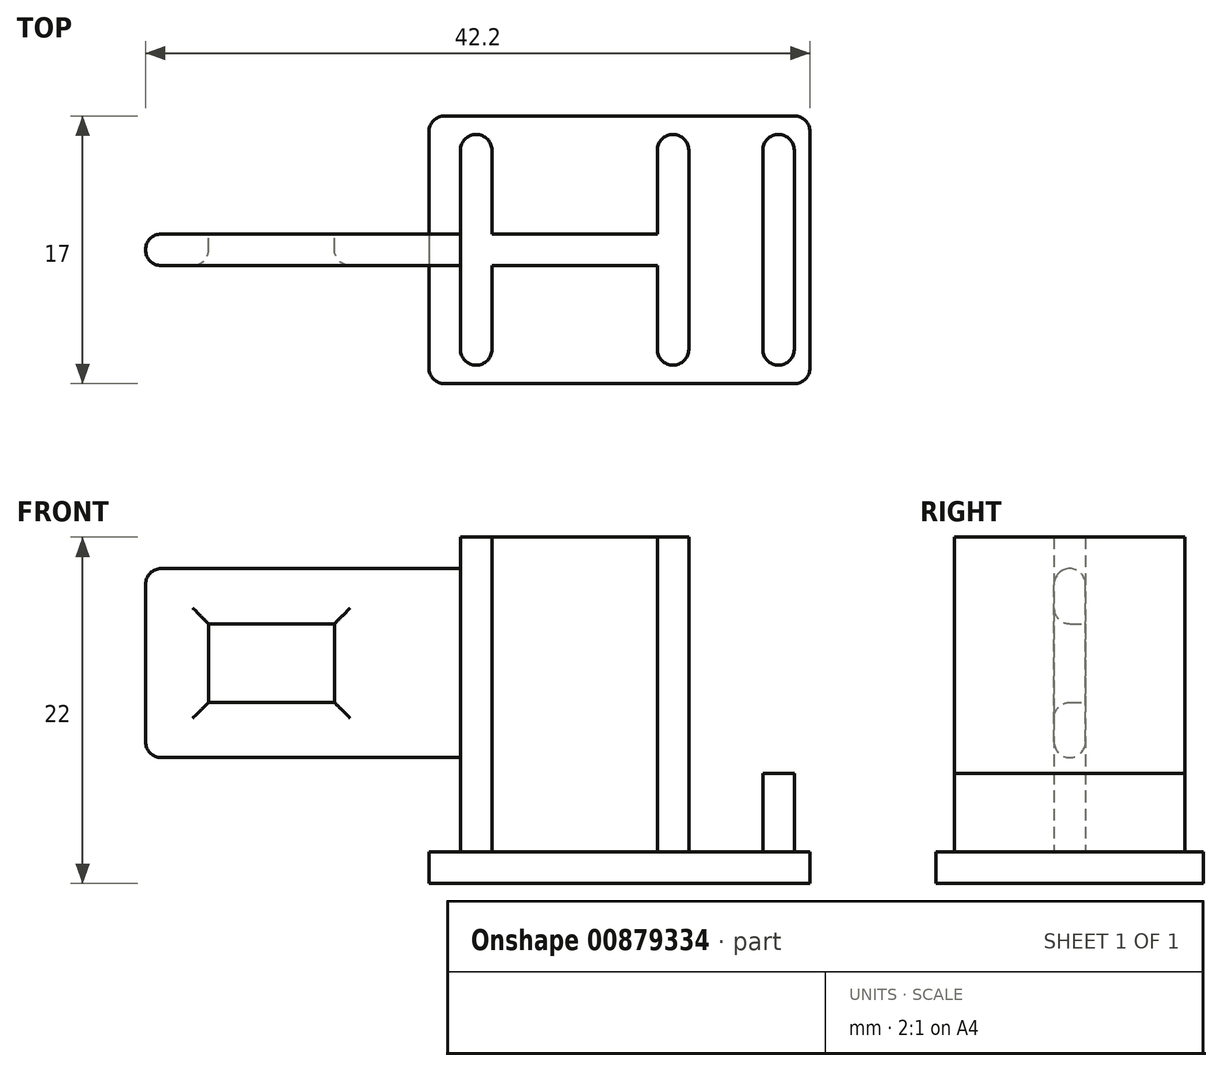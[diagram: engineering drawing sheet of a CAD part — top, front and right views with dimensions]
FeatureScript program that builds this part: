
annotation { "Feature Type Name" : "Feature", "Feature Type Description" : "" }
export const myFeature = defineFeature(function(context is Context, id is Id, definition is map)
    precondition{}
    {
        {
            var Q0;
            Q0=qCreatedBy(makeId("Top.planeOp"),FACE);
            var sketch = newSketch(context, id + "F0", { "sketchPlane" : qUnion([Q0])});
            skLineSegment(sketch, "E0.bottom", {"start": v(12.1, 8.5) * mm, "end": v(-12.1, 8.5) * mm});
            skLineSegment(sketch, "E0.top", {"start": v(12.1, -8.5) * mm, "end": v(-12.1, -8.5) * mm});
            skLineSegment(sketch, "E0.left", {"start": v(12.1, 8.5) * mm, "end": v(12.1, -8.5) * mm});
            skLineSegment(sketch, "E0.right", {"start": v(-12.1, 8.5) * mm, "end": v(-12.1, -8.5) * mm});
            skPoint(sketch, "E0.middle", {"position": v(0, 0) * mm});
            skLineSegment(sketch, "E1.bottom", {"start": v(9.1, 7.33) * mm, "end": v(11.1, 7.33) * mm});
            skLineSegment(sketch, "E1.top", {"start": v(9.1, -7.32) * mm, "end": v(11.1, -7.32) * mm});
            skLineSegment(sketch, "E1.left", {"start": v(9.1, 7.33) * mm, "end": v(9.1, -7.32) * mm});
            skLineSegment(sketch, "E1.right", {"start": v(11.1, 7.33) * mm, "end": v(11.1, -7.32) * mm});
            skPoint(sketch, "E1.middle", {"position": v(10.1, 0) * mm});
            skLineSegment(sketch, "E2.bottom", {"start": v(-8.1, 7.32) * mm, "end": v(-10.1, 7.32) * mm});
            skLineSegment(sketch, "E2.top", {"start": v(-8.1, -7.33) * mm, "end": v(-10.1, -7.33) * mm});
            skLineSegment(sketch, "E2.left", {"start": v(-8.1, 7.32) * mm, "end": v(-8.1, -7.33) * mm});
            skLineSegment(sketch, "E2.right", {"start": v(-10.1, 7.33) * mm, "end": v(-10.1, -7.33) * mm});
            skPoint(sketch, "E2.middle", {"position": v(-9.1, 0) * mm});
            skLineSegment(sketch, "E3.bottom", {"start": v(2.4, 7.33) * mm, "end": v(4.4, 7.33) * mm});
            skLineSegment(sketch, "E3.top", {"start": v(2.4, -7.32) * mm, "end": v(4.4, -7.32) * mm});
            skLineSegment(sketch, "E3.left", {"start": v(2.4, 7.33) * mm, "end": v(2.4, -7.32) * mm});
            skLineSegment(sketch, "E3.right", {"start": v(4.4, 7.33) * mm, "end": v(4.4, -7.32) * mm});
            skPoint(sketch, "E3.middle", {"position": v(3.4, 0) * mm});
            skLineSegment(sketch, "E4.bottom", {"start": v(-8.1, 1) * mm, "end": v(2.4, 1) * mm});
            skLineSegment(sketch, "E4.top", {"start": v(-8.1, -1) * mm, "end": v(2.4, -1) * mm});
            skLineSegment(sketch, "E4.left", {"start": v(-8.1, 1) * mm, "end": v(-8.1, -1) * mm});
            skLineSegment(sketch, "E4.right", {"start": v(2.4, 1) * mm, "end": v(2.4, -1) * mm});
            skPoint(sketch, "E4.middle", {"position": v(-2.85, 0) * mm});
            skLineSegment(sketch, "E5", {"start": v(2.4, 0) * mm, "end": v(-8.1, 0) * mm});
            skSolve(sketch);
        }
        {
            var Q0;
            Q0=makeQuery(id+"F0.imprint","IMPRINT",FACE,{"disambiguationData":[TD([[makeQuery(id+"F0.imprint","IMPRINT",EDGE,{"derivedFrom":sQuery(id+"F0.wireOp",EDGE,"E0.bottom")}),1.0]])]});
            var Q1;
            Q1=makeQuery(id+"F0.imprint","IMPRINT",FACE,{"disambiguationData":[TD([[makeQuery(id+"F0.imprint","IMPRINT",EDGE,{"derivedFrom":sQuery(id+"F0.wireOp",EDGE,"E2.bottom")}),1.0]])]});
            var Q2;
            Q2=makeQuery(id+"F0.imprint","IMPRINT",FACE,{"disambiguationData":[TD([[makeQuery(id+"F0.imprint","IMPRINT",EDGE,{"derivedFrom":sQuery(id+"F0.wireOp",EDGE,"E3.bottom")}),-1.0]])]});
            var Q3;
            Q3=makeQuery(id+"F0.imprint","IMPRINT",FACE,{"disambiguationData":[TD([[makeQuery(id+"F0.imprint","IMPRINT",EDGE,{"derivedFrom":sQuery(id+"F0.wireOp",EDGE,"E1.bottom")}),-1.0]])]});
            var Q4;
            {var subQ0=sQuery(id+"F0.wireOp",EDGE,"E4.top");Q4=makeQuery(id+"F0.imprint","IMPRINT",FACE,{"disambiguationData":[TD([[makeQuery(id+"F0.imprint","IMPRINT",EDGE,{"derivedFrom":subQ0}),1.0]])]});}
            var Q5;
            {var subQ0=sQuery(id+"F0.wireOp",EDGE,"E4.bottom");Q5=makeQuery(id+"F0.imprint","IMPRINT",FACE,{"disambiguationData":[TD([[makeQuery(id+"F0.imprint","IMPRINT",EDGE,{"derivedFrom":subQ0}),-1.0]])]});}
            extrude(context, id + "F1", {"entities" : qUnion([Q0, Q1, Q2, Q3, Q4, Q5]), "oppositeDirection" : true, "depth" : 2 * mm, "offsetDistance" : 25 * mm});
        }
        {
            var Q0;
            {var subQ4=sQuery(id+"F0.wireOp",EDGE,"E2.bottom");Q0=makeQuery(id+"F0.imprint","IMPRINT",FACE,{"disambiguationData":[TD([[makeQuery(id+"F0.imprint","IMPRINT",EDGE,{"derivedFrom":subQ4}),1.0]])]});}
            var Q1;
            {var subQ0=sQuery(id+"F0.wireOp",EDGE,"E4.bottom");Q1=makeQuery(id+"F0.imprint","IMPRINT",FACE,{"disambiguationData":[TD([[makeQuery(id+"F0.imprint","IMPRINT",EDGE,{"derivedFrom":subQ0}),-1.0]])]});}
            var Q2;
            {var subQ4=sQuery(id+"F0.wireOp",EDGE,"E3.bottom");Q2=makeQuery(id+"F0.imprint","IMPRINT",FACE,{"disambiguationData":[TD([[makeQuery(id+"F0.imprint","IMPRINT",EDGE,{"derivedFrom":subQ4}),-1.0]])]});}
            var Q3;
            {var subQ0=sQuery(id+"F0.wireOp",EDGE,"E4.top");Q3=makeQuery(id+"F0.imprint","IMPRINT",FACE,{"disambiguationData":[TD([[makeQuery(id+"F0.imprint","IMPRINT",EDGE,{"derivedFrom":subQ0}),1.0]])]});}
            extrude(context, id + "F2", {"entities" : qUnion([Q0, Q1, Q2, Q3]), "operationType" : NewBodyOperationType.ADD, "depth" : 20 * mm, "offsetDistance" : 25 * mm});
        }
        {
            var Q0;
            Q0=makeQuery(id+"F0.imprint","IMPRINT",FACE,{"disambiguationData":[TD([[makeQuery(id+"F0.imprint","IMPRINT",EDGE,{"derivedFrom":sQuery(id+"F0.wireOp",EDGE,"E1.bottom")}),-1.0]])]});
            extrude(context, id + "F3", {"entities" : qUnion([Q0]), "operationType" : NewBodyOperationType.ADD, "depth" : 5 * mm, "offsetDistance" : 25 * mm});
        }
        {
            var Q0;
            Q0=makeQuery(id+"F2.opExtrude","SWEPT_FACE",FACE,{"disambiguationData":[OSD([sQuery(id+"F0.wireOp",EDGE,"E2.right")])]});
            var sketch = newSketch(context, id + "F4", { "sketchPlane" : qUnion([Q0])});
            skLineSegment(sketch, "E6.bottom", {"start": v(1, 6) * mm, "end": v(-1, 6) * mm});
            skLineSegment(sketch, "E6.top", {"start": v(1, 18) * mm, "end": v(-1, 18) * mm});
            skLineSegment(sketch, "E6.left", {"start": v(1, 6) * mm, "end": v(1, 18) * mm});
            skLineSegment(sketch, "E6.right", {"start": v(-1, 6) * mm, "end": v(-1, 18) * mm});
            skPoint(sketch, "E6.middle", {"position": v(0, 12) * mm});
            skSolve(sketch);
        }
        {
            var Q0;
            Q0 = qSketchRegion(id + "F4", true);
            extrude(context, id + "F5", {"entities" : qUnion([Q0]), "operationType" : NewBodyOperationType.ADD, "depth" : 20 * mm, "offsetDistance" : 25 * mm});
        }
        {
            var Q0;
            Q0=makeQuery(id+"F5.opExtrude","SWEPT_FACE",FACE,{"disambiguationData":[OSD([sQuery(id+"F4.wireOp",EDGE,"E6.right")])]});
            var sketch = newSketch(context, id + "F6", { "sketchPlane" : qUnion([Q0])});
            skLineSegment(sketch, "E7.bottom", {"start": v(26.1, 14.5) * mm, "end": v(18.1, 14.5) * mm});
            skLineSegment(sketch, "E7.top", {"start": v(26.1, 9.5) * mm, "end": v(18.1, 9.5) * mm});
            skLineSegment(sketch, "E7.left", {"start": v(26.1, 14.5) * mm, "end": v(26.1, 9.5) * mm});
            skLineSegment(sketch, "E7.right", {"start": v(18.1, 14.5) * mm, "end": v(18.1, 9.5) * mm});
            skPoint(sketch, "E7.middle", {"position": v(22.1, 12) * mm});
            skPoint(sketch, "E7.middle.positionSnap0", {"position": v(29.1, 12) * mm});
            skPoint(sketch, "E7.centerSnap0", {"position": v(29.1, 12) * mm});
            skSolve(sketch);
        }
        {
            var Q0;
            Q0=makeQuery(id+"F6.imprint","IMPRINT",FACE,{"disambiguationData":[TD([[makeQuery(id+"F6.imprint","IMPRINT",EDGE,{"derivedFrom":sQuery(id+"F6.wireOp",EDGE,"E7.bottom")}),1.0]])]});
            extrude(context, id + "F7", {"entities" : qUnion([Q0]), "operationType" : NewBodyOperationType.REMOVE, "oppositeDirection" : true, "depth" : 25 * mm, "offsetDistance" : 25 * mm});
        }
        {
            var Q0;
            Q0=makeQuery(id+"F1.opExtrude","SWEPT_EDGE",EDGE,{"disambiguationData":[OSD([sQuery(id+"F0.wireOp",EDGE,"E0.top"),sQuery(id+"F0.wireOp",EDGE,"E0.right")])]});
            var Q1;
            Q1=makeQuery(id+"F1.opExtrude","SWEPT_EDGE",EDGE,{"disambiguationData":[OSD([sQuery(id+"F0.wireOp",EDGE,"E0.bottom"),sQuery(id+"F0.wireOp",EDGE,"E0.right")])]});
            var Q2;
            Q2=makeQuery(id+"F1.opExtrude","SWEPT_EDGE",EDGE,{"disambiguationData":[OSD([sQuery(id+"F0.wireOp",EDGE,"E0.top"),sQuery(id+"F0.wireOp",EDGE,"E0.left")])]});
            var Q3;
            Q3=makeQuery(id+"F1.opExtrude","SWEPT_EDGE",EDGE,{"disambiguationData":[OSD([sQuery(id+"F0.wireOp",EDGE,"E0.bottom"),sQuery(id+"F0.wireOp",EDGE,"E0.left")])]});
            var Q4;
            Q4=makeQuery(id+"F3.opExtrude","SWEPT_EDGE",EDGE,{"disambiguationData":[OSD([sQuery(id+"F0.wireOp",EDGE,"E1.top"),sQuery(id+"F0.wireOp",EDGE,"E1.right")])]});
            var Q5;
            Q5=makeQuery(id+"F3.opExtrude","SWEPT_EDGE",EDGE,{"disambiguationData":[OSD([sQuery(id+"F0.wireOp",EDGE,"E1.top"),sQuery(id+"F0.wireOp",EDGE,"E1.left")])]});
            var Q6;
            Q6=makeQuery(id+"F3.opExtrude","SWEPT_EDGE",EDGE,{"disambiguationData":[OSD([sQuery(id+"F0.wireOp",EDGE,"E1.bottom"),sQuery(id+"F0.wireOp",EDGE,"E1.right")])]});
            var Q7;
            Q7=makeQuery(id+"F3.opExtrude","SWEPT_EDGE",EDGE,{"disambiguationData":[OSD([sQuery(id+"F0.wireOp",EDGE,"E1.bottom"),sQuery(id+"F0.wireOp",EDGE,"E1.left")])]});
            var Q8;
            Q8=makeQuery(id+"F2.opExtrude","SWEPT_EDGE",EDGE,{"disambiguationData":[OSD([sQuery(id+"F0.wireOp",EDGE,"E3.top"),sQuery(id+"F0.wireOp",EDGE,"E3.left")])]});
            var Q9;
            Q9=makeQuery(id+"F2.opExtrude","SWEPT_EDGE",EDGE,{"disambiguationData":[OSD([sQuery(id+"F0.wireOp",EDGE,"E3.top"),sQuery(id+"F0.wireOp",EDGE,"E3.right")])]});
            var Q10;
            Q10=makeQuery(id+"F2.opExtrude","SWEPT_EDGE",EDGE,{"disambiguationData":[OSD([sQuery(id+"F0.wireOp",EDGE,"E2.top"),sQuery(id+"F0.wireOp",EDGE,"E2.left")])]});
            var Q11;
            Q11=makeQuery(id+"F2.opExtrude","SWEPT_EDGE",EDGE,{"disambiguationData":[OSD([sQuery(id+"F0.wireOp",EDGE,"E2.top"),sQuery(id+"F0.wireOp",EDGE,"E2.right")])]});
            var Q12;
            Q12=makeQuery(id+"F2.opExtrude","SWEPT_EDGE",EDGE,{"disambiguationData":[OSD([sQuery(id+"F0.wireOp",EDGE,"E2.bottom"),sQuery(id+"F0.wireOp",EDGE,"E2.right")])]});
            var Q13;
            Q13=makeQuery(id+"F2.opExtrude","SWEPT_EDGE",EDGE,{"disambiguationData":[OSD([sQuery(id+"F0.wireOp",EDGE,"E2.bottom"),sQuery(id+"F0.wireOp",EDGE,"E2.left")])]});
            var Q14;
            Q14=makeQuery(id+"F2.opExtrude","SWEPT_EDGE",EDGE,{"disambiguationData":[OSD([sQuery(id+"F0.wireOp",EDGE,"E3.bottom"),sQuery(id+"F0.wireOp",EDGE,"E3.left")])]});
            var Q15;
            Q15=makeQuery(id+"F2.opExtrude","SWEPT_EDGE",EDGE,{"disambiguationData":[OSD([sQuery(id+"F0.wireOp",EDGE,"E3.bottom"),sQuery(id+"F0.wireOp",EDGE,"E3.right")])]});
            var Q16;
            Q16=makeQuery(id+"F5.opExtrude","SWEPT_EDGE",EDGE,{"disambiguationData":[OSD([sQuery(id+"F4.wireOp",EDGE,"E6.top"),sQuery(id+"F4.wireOp",EDGE,"E6.right")])]});
            var Q17;
            Q17=makeQuery(id+"F5.opExtrude","CAP_EDGE",EDGE,{"disambiguationData":[OSD([sQuery(id+"F4.wireOp",EDGE,"E6.right")])],"isStart":false});
            var Q18;
            Q18=makeQuery(id+"F5.opExtrude","CAP_EDGE",EDGE,{"disambiguationData":[OSD([sQuery(id+"F4.wireOp",EDGE,"E6.left")])],"isStart":false});
            var Q19;
            Q19=makeQuery(id+"F5.opExtrude","SWEPT_EDGE",EDGE,{"disambiguationData":[OSD([sQuery(id+"F4.wireOp",EDGE,"E6.bottom"),sQuery(id+"F4.wireOp",EDGE,"E6.right")])]});
            var Q20;
            Q20=makeQuery(id+"F5.opExtrude","CAP_EDGE",EDGE,{"disambiguationData":[OSD([sQuery(id+"F4.wireOp",EDGE,"E6.bottom")])],"isStart":false});
            var Q21;
            Q21=makeQuery(id+"F5.opExtrude","CAP_EDGE",EDGE,{"disambiguationData":[OSD([sQuery(id+"F4.wireOp",EDGE,"E6.top")])],"isStart":false});
            var Q22;
            Q22=makeQuery(id+"F5.opExtrude","SWEPT_EDGE",EDGE,{"disambiguationData":[OSD([sQuery(id+"F4.wireOp",EDGE,"E6.top"),sQuery(id+"F4.wireOp",EDGE,"E6.left")])]});
            var Q23;
            Q23=makeQuery(id+"F5.opExtrude","SWEPT_EDGE",EDGE,{"disambiguationData":[OSD([sQuery(id+"F4.wireOp",EDGE,"E6.bottom"),sQuery(id+"F4.wireOp",EDGE,"E6.left")])]});
            var Q24;
            Q24=makeQuery(id+"F7.boolean.opBoolean","COPY",EDGE,{"derivedFrom":makeQuery(id+"F7.opExtrude","CAP_EDGE",EDGE,{"disambiguationData":[OSD([sQuery(id+"F6.wireOp",EDGE,"E7.bottom")])],"isStart":true})});
            var Q25;
            Q25=makeQuery(id+"F7.boolean.opBoolean","COPY",EDGE,{"derivedFrom":makeQuery(id+"F7.opExtrude","CAP_EDGE",EDGE,{"disambiguationData":[OSD([sQuery(id+"F6.wireOp",EDGE,"E7.right")])],"isStart":true})});
            var Q26;
            Q26=makeQuery(id+"F7.boolean.opBoolean","COPY",EDGE,{"derivedFrom":makeQuery(id+"F7.opExtrude","CAP_EDGE",EDGE,{"disambiguationData":[OSD([sQuery(id+"F6.wireOp",EDGE,"E7.top")])],"isStart":true})});
            var Q27;
            Q27=makeQuery(id+"F7.boolean.opBoolean","COPY",EDGE,{"derivedFrom":makeQuery(id+"F7.opExtrude","CAP_EDGE",EDGE,{"disambiguationData":[OSD([sQuery(id+"F6.wireOp",EDGE,"E7.left")])],"isStart":true})});
            var Q28;
            Q28=makeQuery(id+"F7.boolean.opBoolean","INTERSECT",EDGE,{"derivedFrom":[makeQuery(id+"F5.opExtrude","SWEPT_FACE",FACE,{"disambiguationData":[OSD([sQuery(id+"F4.wireOp",EDGE,"E6.left")])]}),makeQuery(id+"F7.opExtrude","SWEPT_FACE",FACE,{"disambiguationData":[OSD([sQuery(id+"F6.wireOp",EDGE,"E7.right")])]})]});
            var Q29;
            Q29=makeQuery(id+"F7.boolean.opBoolean","INTERSECT",EDGE,{"derivedFrom":[makeQuery(id+"F5.opExtrude","SWEPT_FACE",FACE,{"disambiguationData":[OSD([sQuery(id+"F4.wireOp",EDGE,"E6.left")])]}),makeQuery(id+"F7.opExtrude","SWEPT_FACE",FACE,{"disambiguationData":[OSD([sQuery(id+"F6.wireOp",EDGE,"E7.top")])]})]});
            var Q30;
            Q30=makeQuery(id+"F7.boolean.opBoolean","INTERSECT",EDGE,{"derivedFrom":[makeQuery(id+"F5.opExtrude","SWEPT_FACE",FACE,{"disambiguationData":[OSD([sQuery(id+"F4.wireOp",EDGE,"E6.left")])]}),makeQuery(id+"F7.opExtrude","SWEPT_FACE",FACE,{"disambiguationData":[OSD([sQuery(id+"F6.wireOp",EDGE,"E7.bottom")])]})]});
            var Q31;
            Q31=makeQuery(id+"F7.boolean.opBoolean","INTERSECT",EDGE,{"derivedFrom":[makeQuery(id+"F5.opExtrude","SWEPT_FACE",FACE,{"disambiguationData":[OSD([sQuery(id+"F4.wireOp",EDGE,"E6.left")])]}),makeQuery(id+"F7.opExtrude","SWEPT_FACE",FACE,{"disambiguationData":[OSD([sQuery(id+"F6.wireOp",EDGE,"E7.left")])]})]});
            fillet(context, id + "F8", {"entities" : qUnion([Q0, Q1, Q2, Q3, Q4, Q5, Q6, Q7, Q8, Q9, Q10, Q11, Q12, Q13, Q14, Q15, Q16, Q17, Q18, Q19, Q20, Q21, Q22, Q23, Q24, Q25, Q26, Q27, Q28, Q29, Q30, Q31]), "radius" : 1 * mm, "tangentPropagation" : true, "allowEdgeOverflow" : false});
        }
    });
